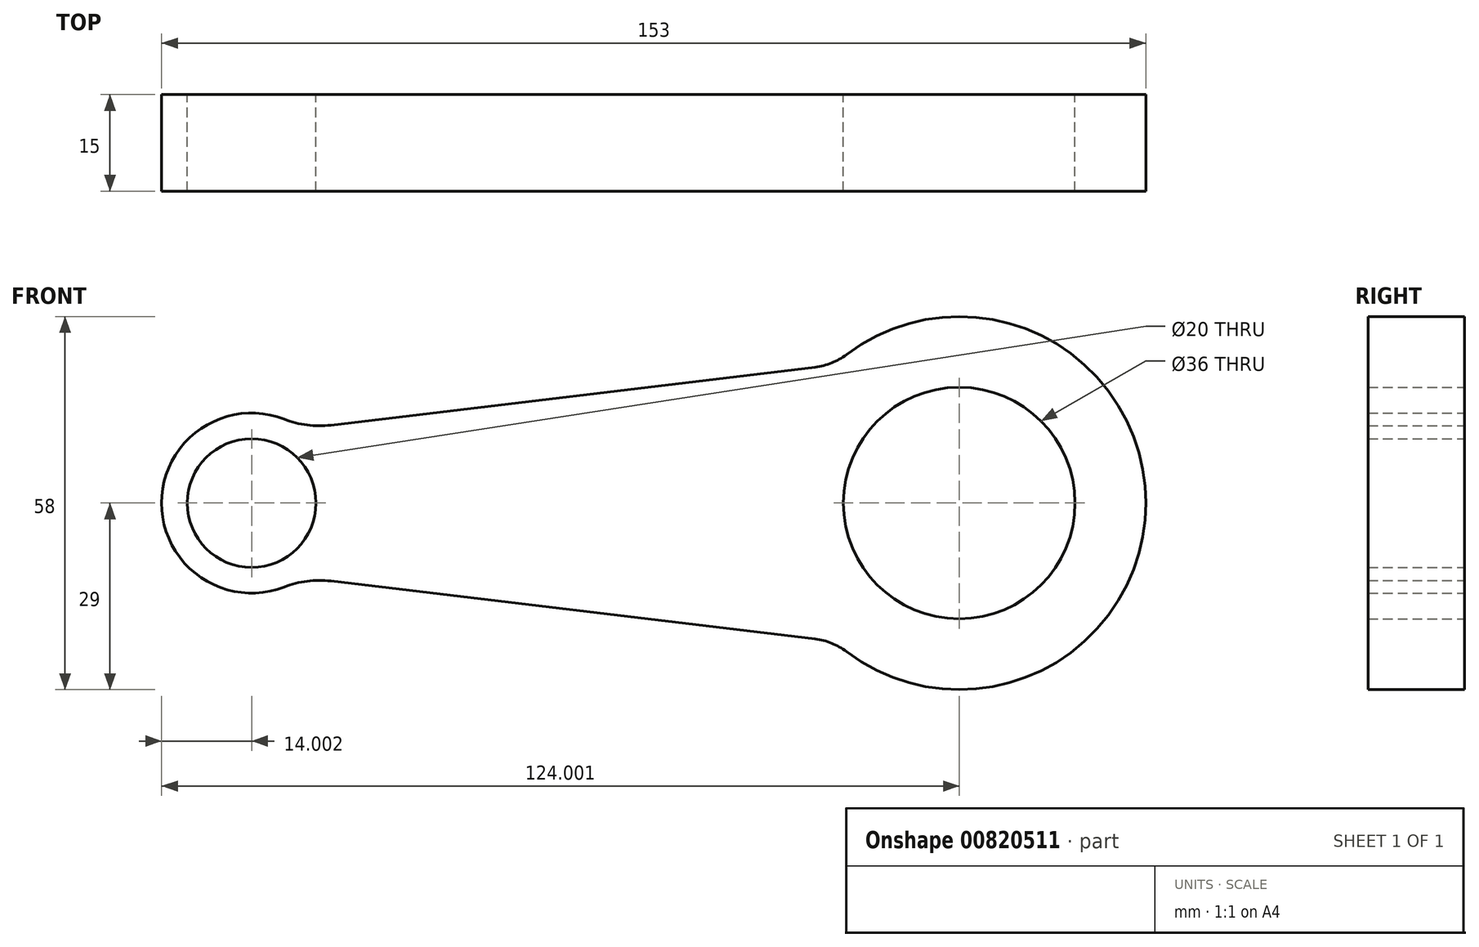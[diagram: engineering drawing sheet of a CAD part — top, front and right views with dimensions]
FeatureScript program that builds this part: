
annotation { "Feature Type Name" : "Feature", "Feature Type Description" : "" }
export const myFeature = defineFeature(function(context is Context, id is Id, definition is map)
    precondition{}
    {
        {
            var Q0;
            Q0=qCreatedBy(makeId("Front.planeOp"),FACE);
            var sketch = newSketch(context, id + "F0", { "sketchPlane" : qUnion([Q0])});
            skCircle(sketch, "E0", {"center": v(-26.88, 0) * mm, "radius": 10 * mm});
            skCircle(sketch, "E1", {"center": v(-26.88, 0) * mm, "radius": 14 * mm});
            skLineSegment(sketch, "E2", {"start": v(-26.88, 0) * mm, "end": v(83.12, 0) * mm});
            skCircle(sketch, "E3", {"center": v(83.12, 0) * mm, "radius": 18 * mm});
            skCircle(sketch, "E4", {"center": v(83.12, 0) * mm, "radius": 29 * mm});
            skLineSegment(sketch, "E5", {"start": v(-19.03, 11.6) * mm, "end": v(63.64, 21.48) * mm});
            skLineSegment(sketch, "E6.MirrorCS", {"start": v(-19.03, -11.6) * mm, "end": v(63.64, -21.48) * mm});
            skSolve(sketch);
        }
        {
            var Q0;
            Q0=makeQuery(id+"F0.imprint","IMPRINT",FACE,{"disambiguationData":[TD([[makeQuery(id+"F0.imprint","IMPRINT",EDGE,{"derivedFrom":sQuery(id+"F0.wireOp",EDGE,"E0")}),-1.0]])]});
            var Q1;
            {var subQ0=sQuery(id+"F0.wireOp",EDGE,"E6.MirrorCS");Q1=makeQuery(id+"F0.imprint","IMPRINT",FACE,{"disambiguationData":[TD([[makeQuery(id+"F0.imprint","IMPRINT",EDGE,{"derivedFrom":subQ0}),1.0]])]});}
            var Q2;
            {var subQ0=sQuery(id+"F0.wireOp",EDGE,"E5");Q2=makeQuery(id+"F0.imprint","IMPRINT",FACE,{"disambiguationData":[TD([[makeQuery(id+"F0.imprint","IMPRINT",EDGE,{"derivedFrom":subQ0}),-1.0]])]});}
            var Q3;
            Q3=makeQuery(id+"F0.imprint","IMPRINT",FACE,{"disambiguationData":[TD([[makeQuery(id+"F0.imprint","IMPRINT",EDGE,{"derivedFrom":sQuery(id+"F0.wireOp",EDGE,"E3")}),-1.0]])]});
            extrude(context, id + "F1", {"entities" : qUnion([Q0, Q1, Q2, Q3]), "endBound" : BoundingType.SYMMETRIC, "depth" : 15 * mm, "offsetDistance" : 25 * mm});
        }
        {
            var Q0;
            Q0=makeQuery(id+"F1.opExtrude","SWEPT_EDGE",EDGE,{"disambiguationData":[OSD([sQuery(id+"F0.wireOp",EDGE,"E4"),sQuery(id+"F0.wireOp",EDGE,"E5")])]});
            fillet(context, id + "F2", {"entities" : qUnion([Q0]), "radius" : 10 * mm, "tangentPropagation" : true, "allowEdgeOverflow" : false});
        }
        {
            var Q0;
            Q0=makeQuery(id+"F1.opExtrude","SWEPT_EDGE",EDGE,{"disambiguationData":[OSD([sQuery(id+"F0.wireOp",EDGE,"E4"),sQuery(id+"F0.wireOp",EDGE,"E6.MirrorCS")])]});
            fillet(context, id + "F3", {"entities" : qUnion([Q0]), "radius" : 10 * mm, "tangentPropagation" : true, "allowEdgeOverflow" : false});
        }
        {
            var Q0;
            Q0=makeQuery(id+"F1.opExtrude","SWEPT_EDGE",EDGE,{"disambiguationData":[OSD([sQuery(id+"F0.wireOp",EDGE,"E1"),sQuery(id+"F0.wireOp",EDGE,"E6.MirrorCS")])]});
            fillet(context, id + "F4", {"entities" : qUnion([Q0]), "radius" : 15 * mm, "tangentPropagation" : true, "allowEdgeOverflow" : false});
        }
        {
            var Q0;
            Q0=makeQuery(id+"F1.opExtrude","SWEPT_EDGE",EDGE,{"disambiguationData":[OSD([sQuery(id+"F0.wireOp",EDGE,"E1"),sQuery(id+"F0.wireOp",EDGE,"E5")])]});
            fillet(context, id + "F5", {"entities" : qUnion([Q0]), "radius" : 15 * mm, "tangentPropagation" : true, "allowEdgeOverflow" : false});
        }
    });
